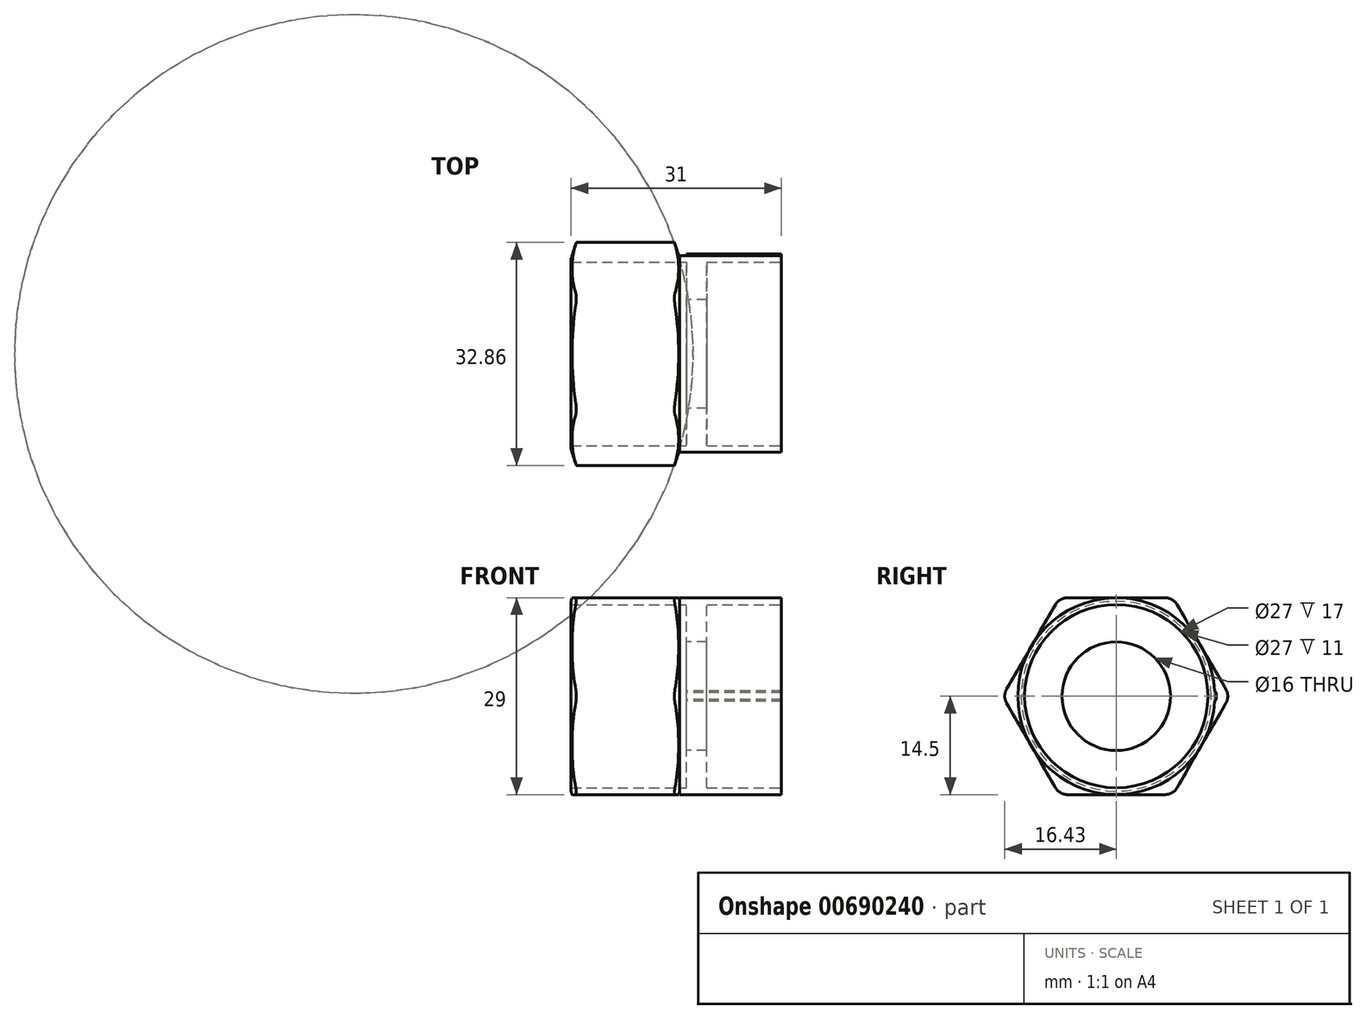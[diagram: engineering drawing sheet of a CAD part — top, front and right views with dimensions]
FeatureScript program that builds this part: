
annotation { "Feature Type Name" : "Feature", "Feature Type Description" : "" }
export const myFeature = defineFeature(function(context is Context, id is Id, definition is map)
    precondition{}
    {
        {
            var Q0;
            Q0=qCreatedBy(makeId("Right.planeOp"),FACE);
            var sketch = newSketch(context, id + "F0", { "sketchPlane" : qUnion([Q0])});
            skCircle(sketch, "E0.cCircle", {"center": v(0, 0) * mm, "radius": 14.5 * mm, "construction": true});
            skLineSegment(sketch, "E0.0", {"start": v(8.37, -14.5) * mm, "end": v(-8.37, -14.5) * mm});
            skLineSegment(sketch, "E0.1", {"start": v(-8.37, -14.5) * mm, "end": v(-16.74, 0) * mm});
            skLineSegment(sketch, "E0.2", {"start": v(-16.74, 0) * mm, "end": v(-8.37, 14.5) * mm});
            skLineSegment(sketch, "E0.3", {"start": v(-8.37, 14.5) * mm, "end": v(8.37, 14.5) * mm});
            skLineSegment(sketch, "E0.4", {"start": v(8.37, 14.5) * mm, "end": v(16.74, 0) * mm});
            skLineSegment(sketch, "E0.5", {"start": v(16.74, 0) * mm, "end": v(8.37, -14.5) * mm});
            skPoint(sketch, "E0.0.midPoint", {"position": v(0, -14.5) * mm});
            skCircle(sketch, "E1", {"center": v(0, 0) * mm, "radius": 13.5 * mm});
            skSolve(sketch);
        }
        {
            var Q0;
            Q0=qSketchRegion(id+"F0",true);
            extrude(context, id + "F1", {"entities" : qUnion([Q0]), "oppositeDirection" : true, "depth" : 16 * mm, "offsetDistance" : 25 * mm});
        }
        {
            var Q0;
            Q0=qSketchRegion(id+"F0",true);
            extrude(context, id + "F2", {"entities" : qUnion([Q0]), "operationType" : NewBodyOperationType.REMOVE, "oppositeDirection" : true, "depth" : 8 * mm, "offsetDistance" : 25 * mm});
        }
        {
            var Q0;
            Q0=qCreatedBy(makeId("Top.planeOp"),FACE);
            var sketch = newSketch(context, id + "F3", { "sketchPlane" : qUnion([Q0])});
            skArc(sketch, "E2", {"start": v(32, 50) * mm, "mid": v(-18, 0) * mm, "end": v(32, -50) * mm});
            skLineSegment(sketch, "E3", {"start": v(32, 50) * mm, "end": v(32, -50) * mm});
            skSolve(sketch);
        }
        {
            var Q0;
            Q0=qSketchRegion(id+"F3",true);
            var Q1;
            Q1=sQuery(id+"F3.wireOp",EDGE,"E3");
            revolve(context, id + "F4", {"entities" : qUnion([Q0]), "axis" : qUnion([Q1]), "revolveType" : RevolveType.FULL});
        }
        {
            var Q0;
            Q0=makeQuery(id+"F4.opRevolve","SWEPT_BODY",BODY,{"disambiguationData":[OSD([sQuery(id+"F3.wireOp",EDGE,"E2"),sQuery(id+"F3.wireOp",EDGE,"E3")])]});
            var Q1;
            Q1=makeQuery(id+"F1.opExtrude","SWEPT_BODY",BODY,{"disambiguationData":[OSD([sQuery(id+"F0.wireOp",EDGE,"E0.0"),sQuery(id+"F0.wireOp",EDGE,"E0.1"),sQuery(id+"F0.wireOp",EDGE,"E0.2"),sQuery(id+"F0.wireOp",EDGE,"E0.3"),sQuery(id+"F0.wireOp",EDGE,"E0.4"),sQuery(id+"F0.wireOp",EDGE,"E0.5"),sQuery(id+"F0.wireOp",EDGE,"E1")])]});
            booleanBodies(context, id + "F5", {"operationType" : BooleanOperationType.INTERSECTION, "tools" : qUnion([Q0, Q1])});
        }
        {
            var Q0;
            Q0=makeQuery(id+"F1.opExtrude","SWEPT_EDGE",EDGE,{"disambiguationData":[OSD([sQuery(id+"F0.wireOp",EDGE,"E0.2"),sQuery(id+"F0.wireOp",EDGE,"E0.3")])]});
            var Q1;
            Q1=makeQuery(id+"F1.opExtrude","SWEPT_EDGE",EDGE,{"disambiguationData":[OSD([sQuery(id+"F0.wireOp",EDGE,"E0.3"),sQuery(id+"F0.wireOp",EDGE,"E0.4")])]});
            var Q2;
            Q2=makeQuery(id+"F1.opExtrude","SWEPT_EDGE",EDGE,{"disambiguationData":[OSD([sQuery(id+"F0.wireOp",EDGE,"E0.4"),sQuery(id+"F0.wireOp",EDGE,"E0.5")])]});
            var Q3;
            Q3=makeQuery(id+"F1.opExtrude","SWEPT_EDGE",EDGE,{"disambiguationData":[OSD([sQuery(id+"F0.wireOp",EDGE,"E0.0"),sQuery(id+"F0.wireOp",EDGE,"E0.5")])]});
            var Q4;
            Q4=makeQuery(id+"F1.opExtrude","SWEPT_EDGE",EDGE,{"disambiguationData":[OSD([sQuery(id+"F0.wireOp",EDGE,"E0.0"),sQuery(id+"F0.wireOp",EDGE,"E0.1")])]});
            var Q5;
            Q5=makeQuery(id+"F1.opExtrude","SWEPT_EDGE",EDGE,{"disambiguationData":[OSD([sQuery(id+"F0.wireOp",EDGE,"E0.1"),sQuery(id+"F0.wireOp",EDGE,"E0.2")])]});
            fillet(context, id + "F6", {"entities" : qUnion([Q0, Q1, Q2, Q3, Q4, Q5]), "radius" : 2 * mm, "tangentPropagation" : true, "allowEdgeOverflow" : false});
        }
        {
            var Q0;
            Q0=makeQuery(id+"F5.opBoolean","INTERSECT",BODY,{"derivedFrom":[makeQuery(id+"F1.opExtrude","SWEPT_BODY",BODY,{"disambiguationData":[OSD([sQuery(id+"F0.wireOp",EDGE,"E0.0"),sQuery(id+"F0.wireOp",EDGE,"E0.1"),sQuery(id+"F0.wireOp",EDGE,"E0.2"),sQuery(id+"F0.wireOp",EDGE,"E0.3"),sQuery(id+"F0.wireOp",EDGE,"E0.4"),sQuery(id+"F0.wireOp",EDGE,"E0.5"),sQuery(id+"F0.wireOp",EDGE,"E1")])]}),makeQuery(id+"F4.opRevolve","SWEPT_BODY",BODY,{"disambiguationData":[OSD([sQuery(id+"F3.wireOp",EDGE,"E2"),sQuery(id+"F3.wireOp",EDGE,"E3")])]})]});
            var Q1;
            Q1=makeQuery(id+"F2.boolean.opBoolean","COPY",FACE,{"derivedFrom":makeQuery(id+"F2.opExtrude","CAP_FACE",FACE,{"disambiguationData":[OSD([sQuery(id+"F0.wireOp",EDGE,"E0.0"),sQuery(id+"F0.wireOp",EDGE,"E0.1"),sQuery(id+"F0.wireOp",EDGE,"E0.2"),sQuery(id+"F0.wireOp",EDGE,"E0.3"),sQuery(id+"F0.wireOp",EDGE,"E0.4"),sQuery(id+"F0.wireOp",EDGE,"E0.5"),sQuery(id+"F0.wireOp",EDGE,"E1")])],"isStart":false})});
            mirror(context, id + "F7", {"operationType" : NewBodyOperationType.ADD, "entities" : qUnion([Q0]), "mirrorPlane" : qUnion([Q1])});
        }
        {
            var Q0;
            Q0=qCreatedBy(makeId("Right.planeOp"),FACE);
            cPlane(context, id + "F8", {"entities" : qUnion([Q0]), "cplaneType" : CPlaneType.OFFSET, "offset" : 1 * mm, "width" : 150 * mm, "height" : 150 * mm});
        }
        {
            var Q0;
            Q0=qCreatedBy(makeId("Right.planeOp"),FACE);
            var sketch = newSketch(context, id + "F9", { "sketchPlane" : qUnion([Q0])});
            skCircle(sketch, "E4", {"center": v(0, 0) * mm, "radius": 14.5 * mm});
            skCircle(sketch, "E5", {"center": v(0, 0) * mm, "radius": 13.5 * mm});
            skSolve(sketch);
        }
        {
            var Q0;
            Q0=makeQuery(id+"F9.imprint","IMPRINT",FACE,{"disambiguationData":[TD([[makeQuery(id+"F9.imprint","IMPRINT",EDGE,{"derivedFrom":sQuery(id+"F9.wireOp",EDGE,"E5")}),-1.0]])]});
            extrude(context, id + "F10", {"entities" : qUnion([Q0]), "operationType" : NewBodyOperationType.ADD, "depth" : 15 * mm, "offsetDistance" : 25 * mm});
        }
        {
            var Q0;
            Q0=qCreatedBy(id+"F8.planeOp",FACE);
            var sketch = newSketch(context, id + "F11", { "sketchPlane" : qUnion([Q0])});
            skCircle(sketch, "E6", {"center": v(0, 0) * mm, "radius": 8 * mm});
            skCircle(sketch, "E7", {"center": v(0, 0) * mm, "radius": 13.5 * mm});
            skSolve(sketch);
        }
        {
            var Q0;
            Q0=qSketchRegion(id+"F11",true);
            extrude(context, id + "F12", {"entities" : qUnion([Q0]), "operationType" : NewBodyOperationType.ADD, "depth" : 3 * mm, "offsetDistance" : 25 * mm});
        }
        {
            var Q0;
            Q0=qCreatedBy(id+"F8.planeOp",FACE);
            var sketch = newSketch(context, id + "F13", { "sketchPlane" : qUnion([Q0])});
            skLineSegment(sketch, "E8", {"start": v(14.48, 0.75) * mm, "end": v(14.73, 0.5) * mm});
            skLineSegment(sketch, "E9", {"start": v(14.73, 0.5) * mm, "end": v(14.73, 0) * mm});
            skLineSegment(sketch, "E10.MirrorCS", {"start": v(14.73, -0.5) * mm, "end": v(14.73, 0) * mm});
            skLineSegment(sketch, "E11.MirrorCS", {"start": v(14.48, -0.75) * mm, "end": v(14.73, -0.5) * mm});
            skCircle(sketch, "E12", {"center": v(0, 0) * mm, "radius": 14.5 * mm});
            skSolve(sketch);
        }
        {
            var Q0;
            {var subQ1=sQuery(id+"F13.wireOp",EDGE,"E8");Q0=makeQuery(id+"F13.imprint","IMPRINT",FACE,{"disambiguationData":[TD([[makeQuery(id+"F13.imprint","IMPRINT",EDGE,{"derivedFrom":subQ1}),-1.0]])]});}
            var Q1;
            Q1=makeQuery(id+"F10.opExtrude","CAP_FACE",FACE,{"disambiguationData":[OSD([sQuery(id+"F9.wireOp",EDGE,"E4"),sQuery(id+"F9.wireOp",EDGE,"E5")])],"isStart":false});
            extrude(context, id + "F14", {"entities" : qUnion([Q0]), "operationType" : NewBodyOperationType.ADD, "endBound" : BoundingType.UP_TO_SURFACE, "depth" : 25 * mm, "endBoundEntityFace" : qUnion([Q1]), "offsetDistance" : 25 * mm});
        }
    });
